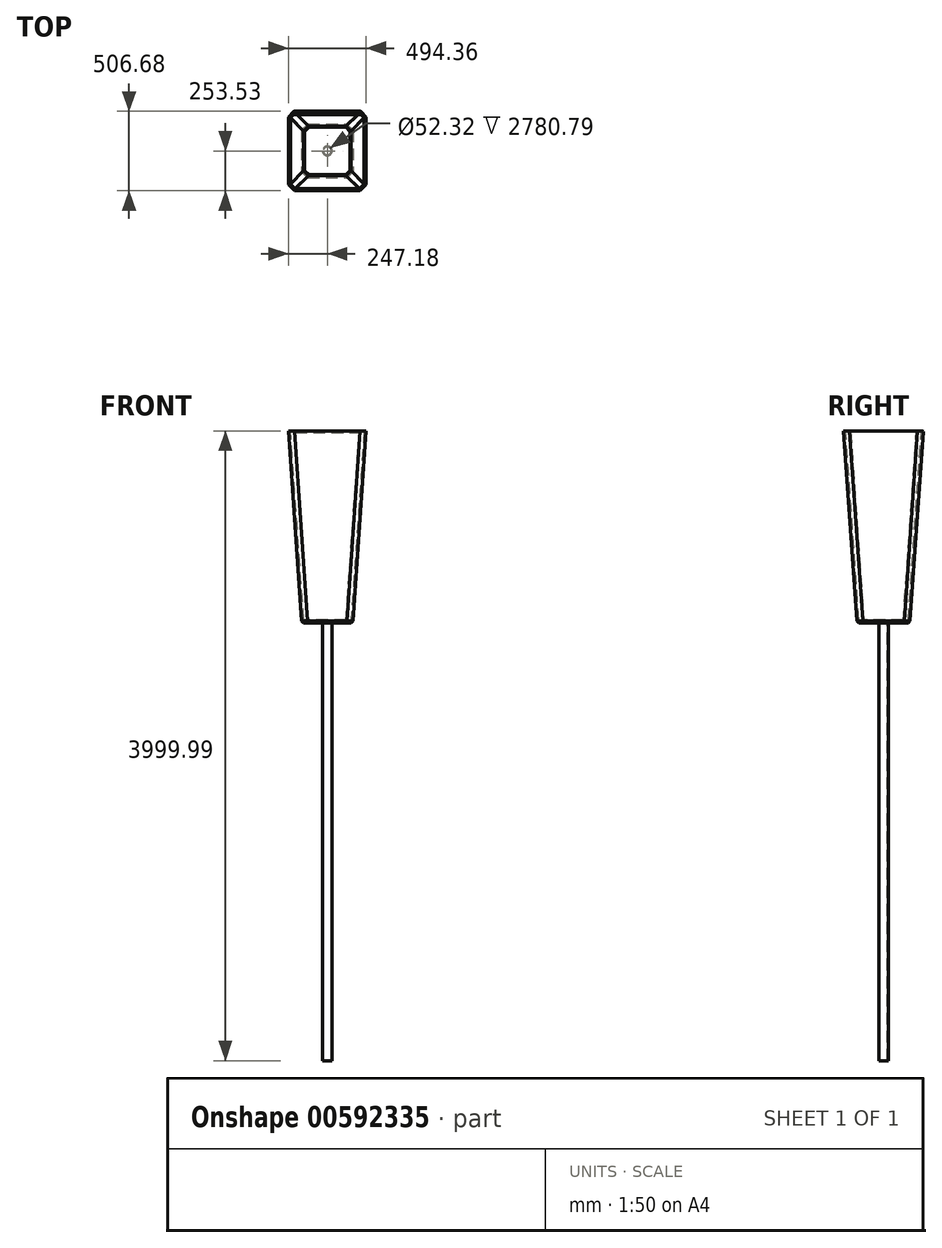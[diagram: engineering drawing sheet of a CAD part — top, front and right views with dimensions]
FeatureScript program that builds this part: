
annotation { "Feature Type Name" : "Feature", "Feature Type Description" : "" }
export const myFeature = defineFeature(function(context is Context, id is Id, definition is map)
    precondition{}
    {
        {
            var Q0;
            Q0=qCreatedBy(makeId("Top.planeOp"),FACE);
            var sketch = newSketch(context, id + "F0", { "sketchPlane" : qUnion([Q0])});
            skLineSegment(sketch, "E0.bottom", {"start": v(161.93, -168.27) * mm, "end": v(-161.92, -168.28) * mm});
            skLineSegment(sketch, "E0.top", {"start": v(161.92, 168.28) * mm, "end": v(-161.93, 168.27) * mm});
            skLineSegment(sketch, "E0.left", {"start": v(161.93, -168.27) * mm, "end": v(161.92, 168.28) * mm});
            skLineSegment(sketch, "E0.right", {"start": v(-161.92, -168.28) * mm, "end": v(-161.93, 168.27) * mm});
            skPoint(sketch, "E0.middle", {"position": v(0, 0) * mm});
            skSolve(sketch);
        }
        {
            var Q0;
            Q0 = qSketchRegion(id + "F0", true);
            extrude(context, id + "F1", {"entities" : qUnion([Q0]), "depth" : 1219.2 * mm, "offsetDistance" : 25.4 * mm, "hasDraft" : true, "draftAngle" : 4 * degree});
        }
        {
            var Q0;
            Q0=makeQuery(id+"F1.opExtrude","SWEPT_EDGE",EDGE,{"disambiguationData":[OSD([sQuery(id+"F0.wireOp",EDGE,"E0.bottom"),sQuery(id+"F0.wireOp",EDGE,"E0.right")])]});
            var Q1;
            Q1=makeQuery(id+"F1.opExtrude","SWEPT_EDGE",EDGE,{"disambiguationData":[OSD([sQuery(id+"F0.wireOp",EDGE,"E0.top"),sQuery(id+"F0.wireOp",EDGE,"E0.right")])]});
            var Q2;
            Q2=makeQuery(id+"F1.opExtrude","SWEPT_EDGE",EDGE,{"disambiguationData":[OSD([sQuery(id+"F0.wireOp",EDGE,"E0.top"),sQuery(id+"F0.wireOp",EDGE,"E0.left")])]});
            var Q3;
            Q3=makeQuery(id+"F1.opExtrude","SWEPT_EDGE",EDGE,{"disambiguationData":[OSD([sQuery(id+"F0.wireOp",EDGE,"E0.bottom"),sQuery(id+"F0.wireOp",EDGE,"E0.left")])]});
            chamfer(context, id + "F2", {"entities" : qUnion([Q0, Q1, Q2, Q3]), "width" : 38.1 * mm, "tangentPropagation" : true});
        }
        {
            var Q0;
            Q0=makeQuery(id+"F1.opExtrude","CAP_FACE",FACE,{"disambiguationData":[OSD([sQuery(id+"F0.wireOp",EDGE,"E0.bottom"),sQuery(id+"F0.wireOp",EDGE,"E0.top"),sQuery(id+"F0.wireOp",EDGE,"E0.left"),sQuery(id+"F0.wireOp",EDGE,"E0.right")])],"isStart":true});
            var sketch = newSketch(context, id + "F3", { "sketchPlane" : qUnion([Q0])});
            skCircle(sketch, "E1", {"center": v(0, 0) * mm, "radius": 30.1 * mm});
            skCircle(sketch, "E2", {"center": v(0, 0) * mm, "radius": 26.16 * mm});
            skSolve(sketch);
        }
        {
            var Q0;
            Q0 = qSketchRegion(id + "F3", true);
            extrude(context, id + "F4", {"entities" : qUnion([Q0]), "operationType" : NewBodyOperationType.ADD, "depth" : 2780.8 * mm, "offsetDistance" : 25.4 * mm, "hasSecondDirection" : true, "secondDirectionOppositeDirection" : true, "secondDirectionDepth" : 1219.2 * mm});
        }
        {
            var Q0;
            Q0=makeQuery(id+"F1.opExtrude","CAP_EDGE",EDGE,{"disambiguationData":[OSD([sQuery(id+"F0.wireOp",EDGE,"E0.top")])],"isStart":true});
            var Q1;
            {var subQ0=sQuery(id+"F0.wireOp",EDGE,"E0.right");var subQ1=sQuery(id+"F0.wireOp",EDGE,"E0.top");Q1=makeQuery(id+"F2.opChamfer","BLEND_EDGE",EDGE,{"blendedFrom":[makeQuery(id+"F1.opExtrude","SWEPT_EDGE",EDGE,{"disambiguationData":[OSD([subQ1,subQ0])]}),makeQuery(id+"F1.opExtrude","CAP_FACE",FACE,{"disambiguationData":[OSD([sQuery(id+"F0.wireOp",EDGE,"E0.bottom"),subQ1,sQuery(id+"F0.wireOp",EDGE,"E0.left"),subQ0])],"isStart":true})],"blendedInto":[makeQuery(id+"F1.opExtrude","CAP_FACE",FACE,{"disambiguationData":[OSD([sQuery(id+"F0.wireOp",EDGE,"E0.bottom"),subQ1,sQuery(id+"F0.wireOp",EDGE,"E0.left"),subQ0])],"isStart":true})]});}
            var Q2;
            Q2=makeQuery(id+"F1.opExtrude","CAP_EDGE",EDGE,{"disambiguationData":[OSD([sQuery(id+"F0.wireOp",EDGE,"E0.right")])],"isStart":true});
            var Q3;
            {var subQ0=sQuery(id+"F0.wireOp",EDGE,"E0.right");var subQ1=sQuery(id+"F0.wireOp",EDGE,"E0.bottom");Q3=makeQuery(id+"F2.opChamfer","BLEND_EDGE",EDGE,{"blendedFrom":[makeQuery(id+"F1.opExtrude","SWEPT_EDGE",EDGE,{"disambiguationData":[OSD([subQ1,subQ0])]}),makeQuery(id+"F1.opExtrude","CAP_FACE",FACE,{"disambiguationData":[OSD([subQ1,sQuery(id+"F0.wireOp",EDGE,"E0.top"),sQuery(id+"F0.wireOp",EDGE,"E0.left"),subQ0])],"isStart":true})],"blendedInto":[makeQuery(id+"F1.opExtrude","CAP_FACE",FACE,{"disambiguationData":[OSD([subQ1,sQuery(id+"F0.wireOp",EDGE,"E0.top"),sQuery(id+"F0.wireOp",EDGE,"E0.left"),subQ0])],"isStart":true})]});}
            var Q4;
            Q4=makeQuery(id+"F1.opExtrude","CAP_EDGE",EDGE,{"disambiguationData":[OSD([sQuery(id+"F0.wireOp",EDGE,"E0.bottom")])],"isStart":true});
            var Q5;
            Q5=makeQuery(id+"F1.opExtrude","CAP_EDGE",EDGE,{"disambiguationData":[OSD([sQuery(id+"F0.wireOp",EDGE,"E0.left")])],"isStart":true});
            var Q6;
            {var subQ0=sQuery(id+"F0.wireOp",EDGE,"E0.left");var subQ1=sQuery(id+"F0.wireOp",EDGE,"E0.top");Q6=makeQuery(id+"F2.opChamfer","BLEND_EDGE",EDGE,{"blendedFrom":[makeQuery(id+"F1.opExtrude","SWEPT_EDGE",EDGE,{"disambiguationData":[OSD([subQ1,subQ0])]}),makeQuery(id+"F1.opExtrude","CAP_FACE",FACE,{"disambiguationData":[OSD([sQuery(id+"F0.wireOp",EDGE,"E0.bottom"),subQ1,subQ0,sQuery(id+"F0.wireOp",EDGE,"E0.right")])],"isStart":true})],"blendedInto":[makeQuery(id+"F1.opExtrude","CAP_FACE",FACE,{"disambiguationData":[OSD([sQuery(id+"F0.wireOp",EDGE,"E0.bottom"),subQ1,subQ0,sQuery(id+"F0.wireOp",EDGE,"E0.right")])],"isStart":true})]});}
            var Q7;
            {var subQ0=sQuery(id+"F0.wireOp",EDGE,"E0.left");var subQ1=sQuery(id+"F0.wireOp",EDGE,"E0.bottom");Q7=makeQuery(id+"F2.opChamfer","BLEND_EDGE",EDGE,{"blendedFrom":[makeQuery(id+"F1.opExtrude","SWEPT_EDGE",EDGE,{"disambiguationData":[OSD([subQ1,subQ0])]}),makeQuery(id+"F1.opExtrude","CAP_FACE",FACE,{"disambiguationData":[OSD([subQ1,sQuery(id+"F0.wireOp",EDGE,"E0.top"),subQ0,sQuery(id+"F0.wireOp",EDGE,"E0.right")])],"isStart":true})],"blendedInto":[makeQuery(id+"F1.opExtrude","CAP_FACE",FACE,{"disambiguationData":[OSD([subQ1,sQuery(id+"F0.wireOp",EDGE,"E0.top"),subQ0,sQuery(id+"F0.wireOp",EDGE,"E0.right")])],"isStart":true})]});}
            chamfer(context, id + "F5", {"entities" : qUnion([Q0, Q1, Q2, Q3, Q4, Q5, Q6, Q7]), "width" : 12.7 * mm, "tangentPropagation" : true});
        }
        {
            var Q0;
            Q0=makeQuery(id+"F1.opExtrude","SWEPT_FACE",FACE,{"disambiguationData":[OSD([sQuery(id+"F0.wireOp",EDGE,"E0.top")])]});
            var Q1;
            {var subQ0=sQuery(id+"F0.wireOp",EDGE,"E0.right");var subQ1=sQuery(id+"F0.wireOp",EDGE,"E0.top");Q1=makeQuery(id+"F2.opChamfer","BLEND_EDGE",EDGE,{"blendedFrom":[makeQuery(id+"F1.opExtrude","SWEPT_EDGE",EDGE,{"disambiguationData":[OSD([subQ1,subQ0])]}),makeQuery(id+"F1.opExtrude","CAP_FACE",FACE,{"disambiguationData":[OSD([sQuery(id+"F0.wireOp",EDGE,"E0.bottom"),subQ1,sQuery(id+"F0.wireOp",EDGE,"E0.left"),subQ0])],"isStart":true})],"blendedInto":[makeQuery(id+"F1.opExtrude","CAP_FACE",FACE,{"disambiguationData":[OSD([sQuery(id+"F0.wireOp",EDGE,"E0.bottom"),subQ1,sQuery(id+"F0.wireOp",EDGE,"E0.left"),subQ0])],"isStart":true})]});}
            var Q2;
            {var subQ0=sQuery(id+"F0.wireOp",EDGE,"E0.left");var subQ1=sQuery(id+"F0.wireOp",EDGE,"E0.top");Q2=makeQuery(id+"F2.opChamfer","BLEND_EDGE",EDGE,{"blendedFrom":[makeQuery(id+"F1.opExtrude","SWEPT_EDGE",EDGE,{"disambiguationData":[OSD([subQ1,subQ0])]}),makeQuery(id+"F1.opExtrude","CAP_FACE",FACE,{"disambiguationData":[OSD([sQuery(id+"F0.wireOp",EDGE,"E0.bottom"),subQ1,subQ0,sQuery(id+"F0.wireOp",EDGE,"E0.right")])],"isStart":true})],"blendedInto":[makeQuery(id+"F1.opExtrude","CAP_FACE",FACE,{"disambiguationData":[OSD([sQuery(id+"F0.wireOp",EDGE,"E0.bottom"),subQ1,subQ0,sQuery(id+"F0.wireOp",EDGE,"E0.right")])],"isStart":true})]});}
            var Q3;
            Q3=makeQuery(id+"F1.opExtrude","CAP_EDGE",EDGE,{"disambiguationData":[OSD([sQuery(id+"F0.wireOp",EDGE,"E0.left")])],"isStart":true});
            var Q4;
            Q4=makeQuery(id+"F1.opExtrude","CAP_EDGE",EDGE,{"disambiguationData":[OSD([sQuery(id+"F0.wireOp",EDGE,"E0.right")])],"isStart":true});
            var Q5;
            {var subQ0=sQuery(id+"F0.wireOp",EDGE,"E0.left");var subQ1=sQuery(id+"F0.wireOp",EDGE,"E0.bottom");Q5=makeQuery(id+"F2.opChamfer","BLEND_EDGE",EDGE,{"blendedFrom":[makeQuery(id+"F1.opExtrude","SWEPT_EDGE",EDGE,{"disambiguationData":[OSD([subQ1,subQ0])]}),makeQuery(id+"F1.opExtrude","CAP_FACE",FACE,{"disambiguationData":[OSD([subQ1,sQuery(id+"F0.wireOp",EDGE,"E0.top"),subQ0,sQuery(id+"F0.wireOp",EDGE,"E0.right")])],"isStart":true})],"blendedInto":[makeQuery(id+"F1.opExtrude","CAP_FACE",FACE,{"disambiguationData":[OSD([subQ1,sQuery(id+"F0.wireOp",EDGE,"E0.top"),subQ0,sQuery(id+"F0.wireOp",EDGE,"E0.right")])],"isStart":true})]});}
            var Q6;
            Q6=makeQuery(id+"F1.opExtrude","CAP_EDGE",EDGE,{"disambiguationData":[OSD([sQuery(id+"F0.wireOp",EDGE,"E0.bottom")])],"isStart":true});
            var Q7;
            {var subQ0=sQuery(id+"F0.wireOp",EDGE,"E0.right");var subQ1=sQuery(id+"F0.wireOp",EDGE,"E0.bottom");Q7=makeQuery(id+"F2.opChamfer","BLEND_EDGE",EDGE,{"blendedFrom":[makeQuery(id+"F1.opExtrude","SWEPT_EDGE",EDGE,{"disambiguationData":[OSD([subQ1,subQ0])]}),makeQuery(id+"F1.opExtrude","CAP_FACE",FACE,{"disambiguationData":[OSD([subQ1,sQuery(id+"F0.wireOp",EDGE,"E0.top"),sQuery(id+"F0.wireOp",EDGE,"E0.left"),subQ0])],"isStart":true})],"blendedInto":[makeQuery(id+"F1.opExtrude","CAP_FACE",FACE,{"disambiguationData":[OSD([subQ1,sQuery(id+"F0.wireOp",EDGE,"E0.top"),sQuery(id+"F0.wireOp",EDGE,"E0.left"),subQ0])],"isStart":true})]});}
            chamfer(context, id + "F6", {"entities" : qUnion([Q0, Q1, Q2, Q3, Q4, Q5, Q6, Q7]), "width" : 5.08 * mm, "tangentPropagation" : true});
        }
        {
            var Q0;
            Q0=makeQuery(id+"F1.opExtrude","CAP_FACE",FACE,{"disambiguationData":[OSD([sQuery(id+"F0.wireOp",EDGE,"E0.bottom"),sQuery(id+"F0.wireOp",EDGE,"E0.top"),sQuery(id+"F0.wireOp",EDGE,"E0.left"),sQuery(id+"F0.wireOp",EDGE,"E0.right")])],"isStart":false});
            shell(context, id + "F7", {"entities" : qUnion([Q0]), "thickness" : 12.7 * mm});
        }
    });
